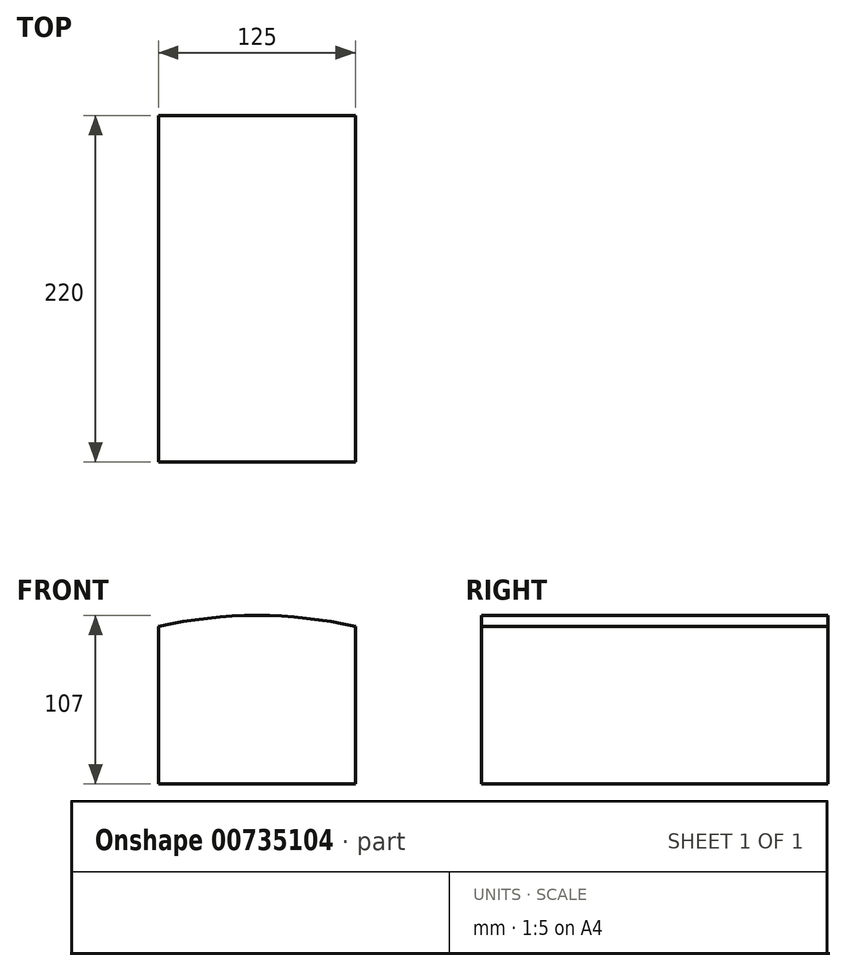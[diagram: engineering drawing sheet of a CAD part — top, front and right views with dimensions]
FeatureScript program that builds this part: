
annotation { "Feature Type Name" : "Feature", "Feature Type Description" : "" }
export const myFeature = defineFeature(function(context is Context, id is Id, definition is map)
    precondition{}
    {
        {
            var Q0;
            Q0=qCreatedBy(makeId("Front.planeOp"),FACE);
            var sketch = newSketch(context, id + "F0", { "sketchPlane" : qUnion([Q0])});
            skLineSegment(sketch, "E0.top", {"start": v(62.5, -50) * mm, "end": v(-62.5, -50) * mm});
            skPoint(sketch, "E0.middle", {"position": v(0, 0) * mm});
            skArc(sketch, "E1", {"start": v(62.5, 50) * mm, "mid": v(0, 57) * mm, "end": v(-62.5, 50) * mm});
            skLineSegment(sketch, "E2", {"start": v(-62.5, 50) * mm, "end": v(-62.5, -50) * mm});
            skLineSegment(sketch, "E3", {"start": v(62.5, 50) * mm, "end": v(62.5, -50) * mm});
            skSolve(sketch);
        }
        {
            var Q0;
            Q0=makeQuery(id+"F0.imprint","IMPRINT",FACE,{"disambiguationData":[TD([[makeQuery(id+"F0.imprint","IMPRINT",EDGE,{"derivedFrom":sQuery(id+"F0.wireOp",EDGE,"E0.top")}),-1.0]])]});
            extrude(context, id + "F1", {"entities" : qUnion([Q0]), "depth" : 220 * mm, "offsetDistance" : 25 * mm});
        }
    });
